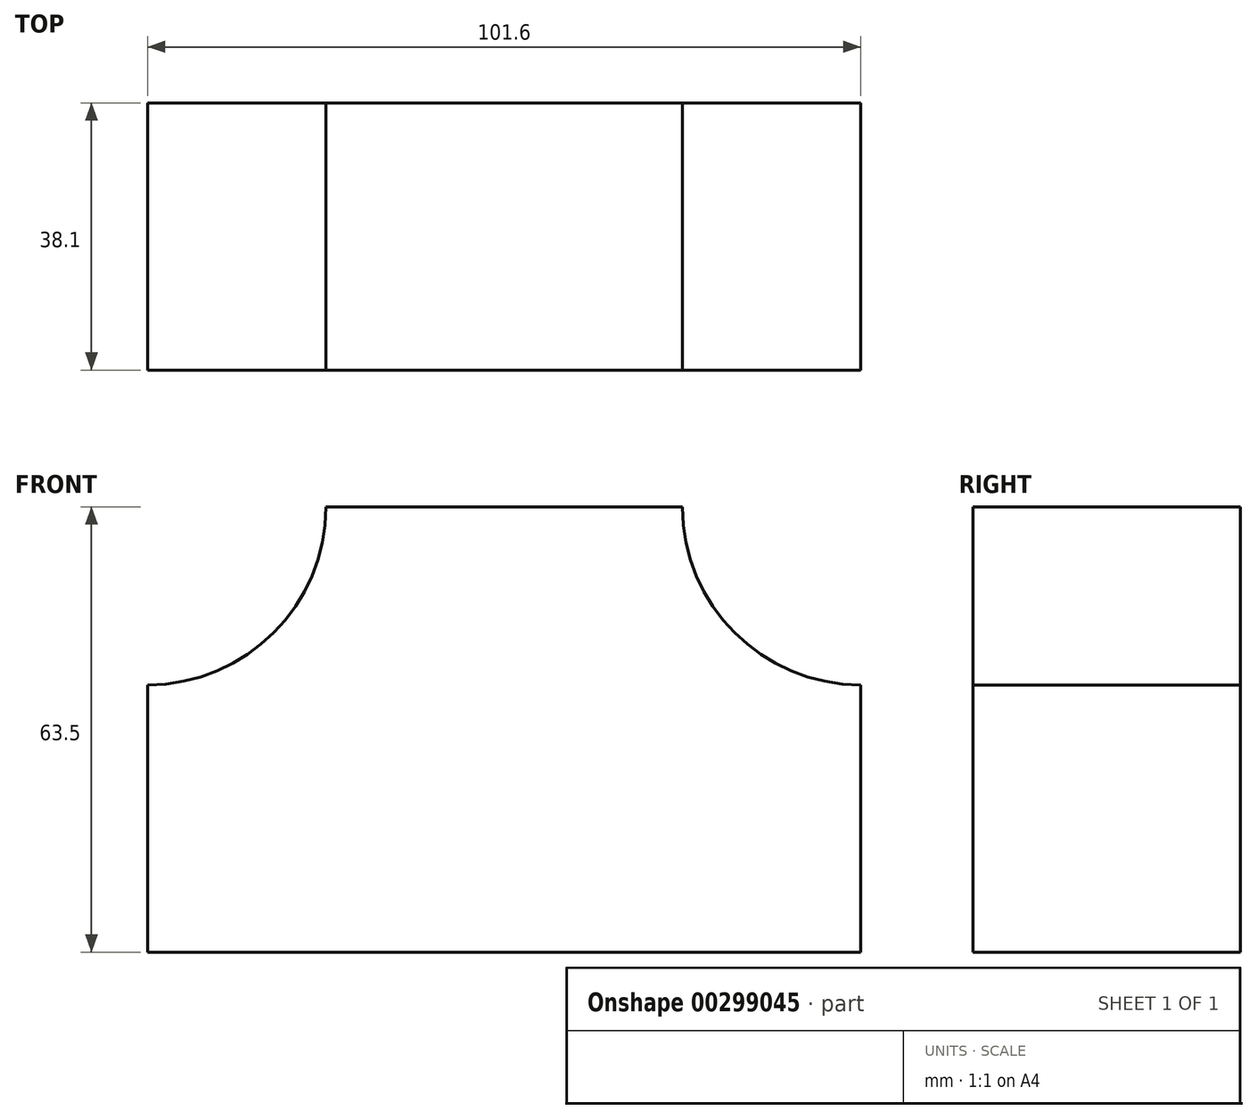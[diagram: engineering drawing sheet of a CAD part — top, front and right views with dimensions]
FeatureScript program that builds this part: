
annotation { "Feature Type Name" : "Feature", "Feature Type Description" : "" }
export const myFeature = defineFeature(function(context is Context, id is Id, definition is map)
    precondition{}
    {
        {
            var Q0;
            Q0=qCreatedBy(makeId("Front.planeOp"),FACE);
            var sketch = newSketch(context, id + "F0", { "sketchPlane" : qUnion([Q0])});
            skLineSegment(sketch, "E0.bottom", {"start": v(56.86, 30.39) * mm, "end": v(-44.74, 30.39) * mm});
            skLineSegment(sketch, "E0.top", {"start": v(56.86, -33.11) * mm, "end": v(-44.74, -33.11) * mm});
            skLineSegment(sketch, "E0.left", {"start": v(56.86, 30.39) * mm, "end": v(56.86, -33.11) * mm});
            skLineSegment(sketch, "E0.right", {"start": v(-44.74, 30.39) * mm, "end": v(-44.74, -33.11) * mm});
            skPoint(sketch, "E0.middle", {"position": v(6.06, -1.36) * mm});
            skSolve(sketch);
        }
        {
            var Q0;
            Q0 = qSketchRegion(id + "F0", true);
            extrude(context, id + "F1", {"entities" : qUnion([Q0]), "depth" : 38.1 * mm});
        }
        {
            var Q0;
            Q0=makeQuery(id+"F1.opExtrude","CAP_FACE",FACE,{"disambiguationData":[OSD([sQuery(id+"F0.wireOp",EDGE,"E0.bottom"),sQuery(id+"F0.wireOp",EDGE,"E0.top"),sQuery(id+"F0.wireOp",EDGE,"E0.left"),sQuery(id+"F0.wireOp",EDGE,"E0.right")])],"isStart":false});
            var sketch = newSketch(context, id + "F2", { "sketchPlane" : qUnion([Q0])});
            skCircle(sketch, "E1", {"center": v(-44.74, 30.39) * mm, "radius": 25.4 * mm});
            skCircle(sketch, "E2", {"center": v(56.86, 30.39) * mm, "radius": 25.4 * mm});
            skSolve(sketch);
        }
        {
            var Q0;
            Q0 = qSketchRegion(id + "F2", true);
            extrude(context, id + "F3", {"entities" : qUnion([Q0]), "operationType" : NewBodyOperationType.REMOVE, "endBound" : BoundingType.THROUGH_ALL, "oppositeDirection" : true, "depth" : 25.4 * mm});
        }
    });
